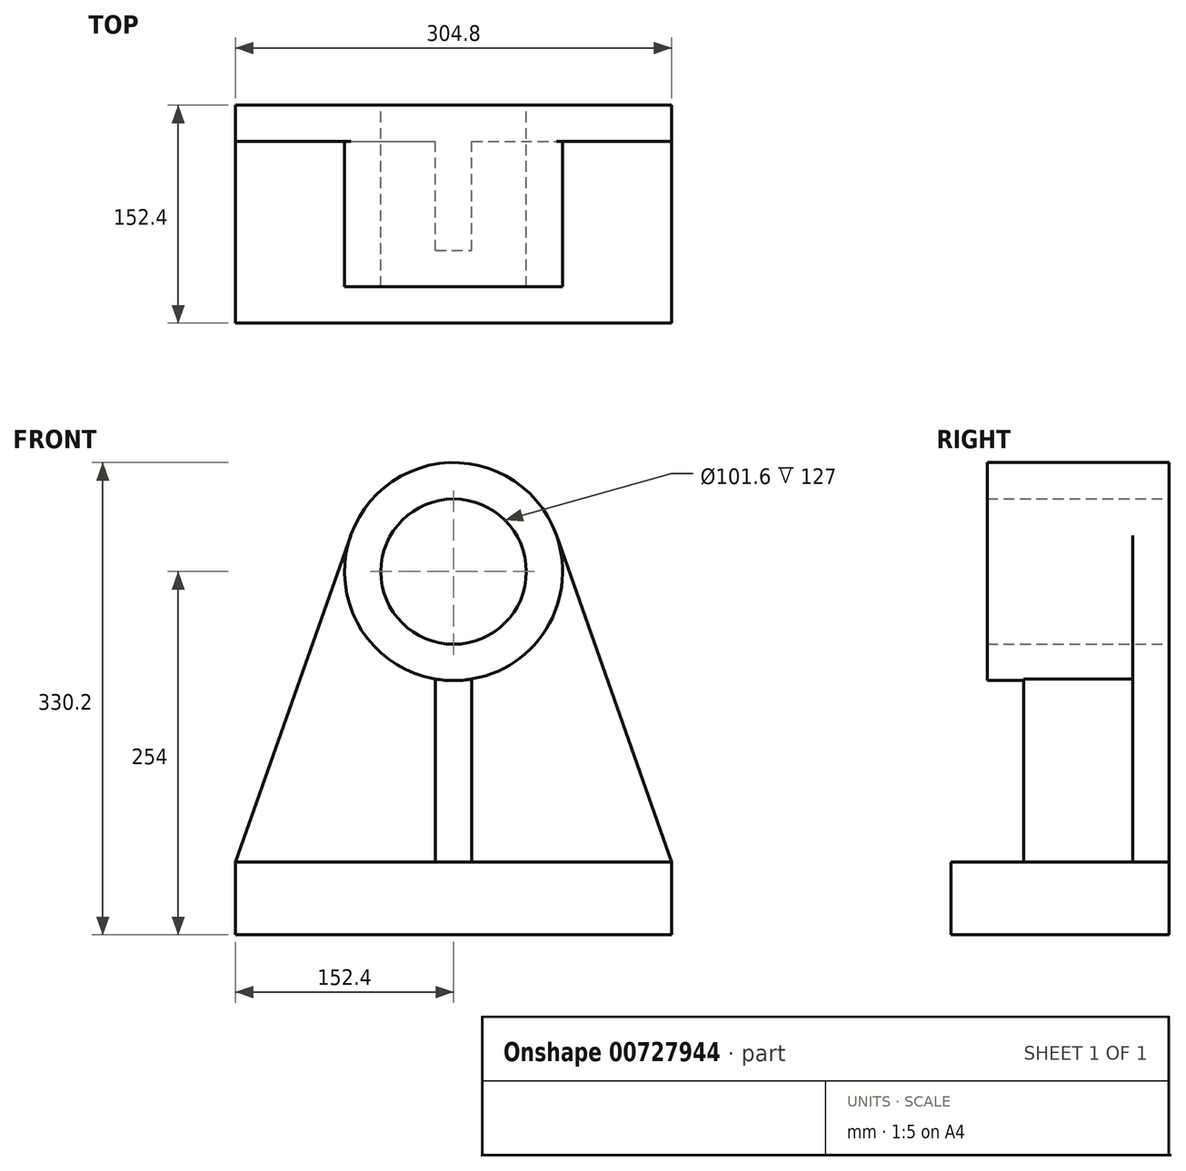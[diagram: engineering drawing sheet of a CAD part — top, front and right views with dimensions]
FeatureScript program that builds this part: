
annotation { "Feature Type Name" : "Feature", "Feature Type Description" : "" }
export const myFeature = defineFeature(function(context is Context, id is Id, definition is map)
    precondition{}
    {
        {
            var Q0;
            Q0=qCreatedBy(makeId("Front.planeOp"),FACE);
            var sketch = newSketch(context, id + "F0", { "sketchPlane" : qUnion([Q0])});
            skCircle(sketch, "E0", {"center": v(0, 0) * mm, "radius": 76.2 * mm});
            skCircle(sketch, "E1", {"center": v(0, 0) * mm, "radius": 50.8 * mm});
            skLineSegment(sketch, "E2", {"start": v(0, 0) * mm, "end": v(0, -228.6) * mm, "construction": true});
            skLineSegment(sketch, "E3.bottom", {"start": v(-152.4, -203.2) * mm, "end": v(152.4, -203.2) * mm});
            skLineSegment(sketch, "E3.top", {"start": v(-152.4, -254) * mm, "end": v(152.4, -254) * mm});
            skLineSegment(sketch, "E3.left", {"start": v(-152.4, -203.2) * mm, "end": v(-152.4, -254) * mm});
            skLineSegment(sketch, "E3.right", {"start": v(152.4, -203.2) * mm, "end": v(152.4, -254) * mm});
            skPoint(sketch, "E3.middle", {"position": v(0, -228.6) * mm});
            skLineSegment(sketch, "E4", {"start": v(-71.87, 25.33) * mm, "end": v(-152.4, -203.2) * mm});
            skLineSegment(sketch, "E5", {"start": v(71.87, 25.33) * mm, "end": v(152.4, -203.2) * mm});
            skLineSegment(sketch, "E6", {"start": v(-12.7, -75.13) * mm, "end": v(-12.7, -203.2) * mm});
            skLineSegment(sketch, "E7", {"start": v(12.7, -75.13) * mm, "end": v(12.7, -203.2) * mm});
            skArc(sketch, "E8", {"start": v(71.87, 25.33) * mm, "mid": v(65.66, -38.67) * mm, "end": v(12.7, -75.13) * mm});
            skArc(sketch, "E9", {"start": v(-71.87, 25.33) * mm, "mid": v(-65.66, -38.67) * mm, "end": v(-12.7, -75.13) * mm});
            skArc(sketch, "E10", {"start": v(-12.7, -75.13) * mm, "mid": v(0, -76.2) * mm, "end": v(12.7, -75.13) * mm});
            skLineSegment(sketch, "E11", {"start": v(-12.7, -203.2) * mm, "end": v(12.7, -203.2) * mm});
            skLineSegment(sketch, "E12", {"start": v(-152.4, -203.2) * mm, "end": v(-12.7, -203.2) * mm});
            skLineSegment(sketch, "E13", {"start": v(12.7, -203.2) * mm, "end": v(152.4, -203.2) * mm});
            skSolve(sketch);
        }
        {
            var Q0;
            Q0=makeQuery(id+"F0.imprint","IMPRINT",FACE,{"disambiguationData":[TD([[makeQuery(id+"F0.imprint","IMPRINT",EDGE,{"derivedFrom":sQuery(id+"F0.wireOp",EDGE,"E1")}),-1.0]])]});
            extrude(context, id + "F1", {"entities" : qUnion([Q0]), "depth" : 127 * mm, "offsetDistance" : 25.4 * mm});
        }
        {
            var Q0;
            {var subQ0=sQuery(id+"F0.wireOp",EDGE,"E4");Q0=makeQuery(id+"F0.imprint","IMPRINT",FACE,{"disambiguationData":[TD([[makeQuery(id+"F0.imprint","IMPRINT",EDGE,{"derivedFrom":subQ0}),1.0]])]});}
            var Q1;
            {var subQ0=sQuery(id+"F0.wireOp",EDGE,"E5");Q1=makeQuery(id+"F0.imprint","IMPRINT",FACE,{"disambiguationData":[TD([[makeQuery(id+"F0.imprint","IMPRINT",EDGE,{"derivedFrom":subQ0}),-1.0]])]});}
            extrude(context, id + "F2", {"entities" : qUnion([Q0, Q1]), "operationType" : NewBodyOperationType.ADD, "depth" : 25.4 * mm, "offsetDistance" : 25.4 * mm});
        }
        {
            var Q0;
            Q0=makeQuery(id+"F0.imprint","IMPRINT",FACE,{"disambiguationData":[TD([[makeQuery(id+"F0.imprint","IMPRINT",EDGE,{"derivedFrom":sQuery(id+"F0.wireOp",EDGE,"E3.top")}),1.0]])]});
            extrude(context, id + "F3", {"entities" : qUnion([Q0]), "operationType" : NewBodyOperationType.ADD, "depth" : 152.4 * mm, "offsetDistance" : 25.4 * mm});
        }
        {
            var Q0;
            {var subQ0=sQuery(id+"F0.wireOp",EDGE,"E6");Q0=makeQuery(id+"F0.imprint","IMPRINT",FACE,{"disambiguationData":[TD([[makeQuery(id+"F0.imprint","IMPRINT",EDGE,{"derivedFrom":subQ0}),1.0]])]});}
            extrude(context, id + "F4", {"entities" : qUnion([Q0]), "operationType" : NewBodyOperationType.ADD, "depth" : 101.6 * mm, "offsetDistance" : 25.4 * mm});
        }
    });
